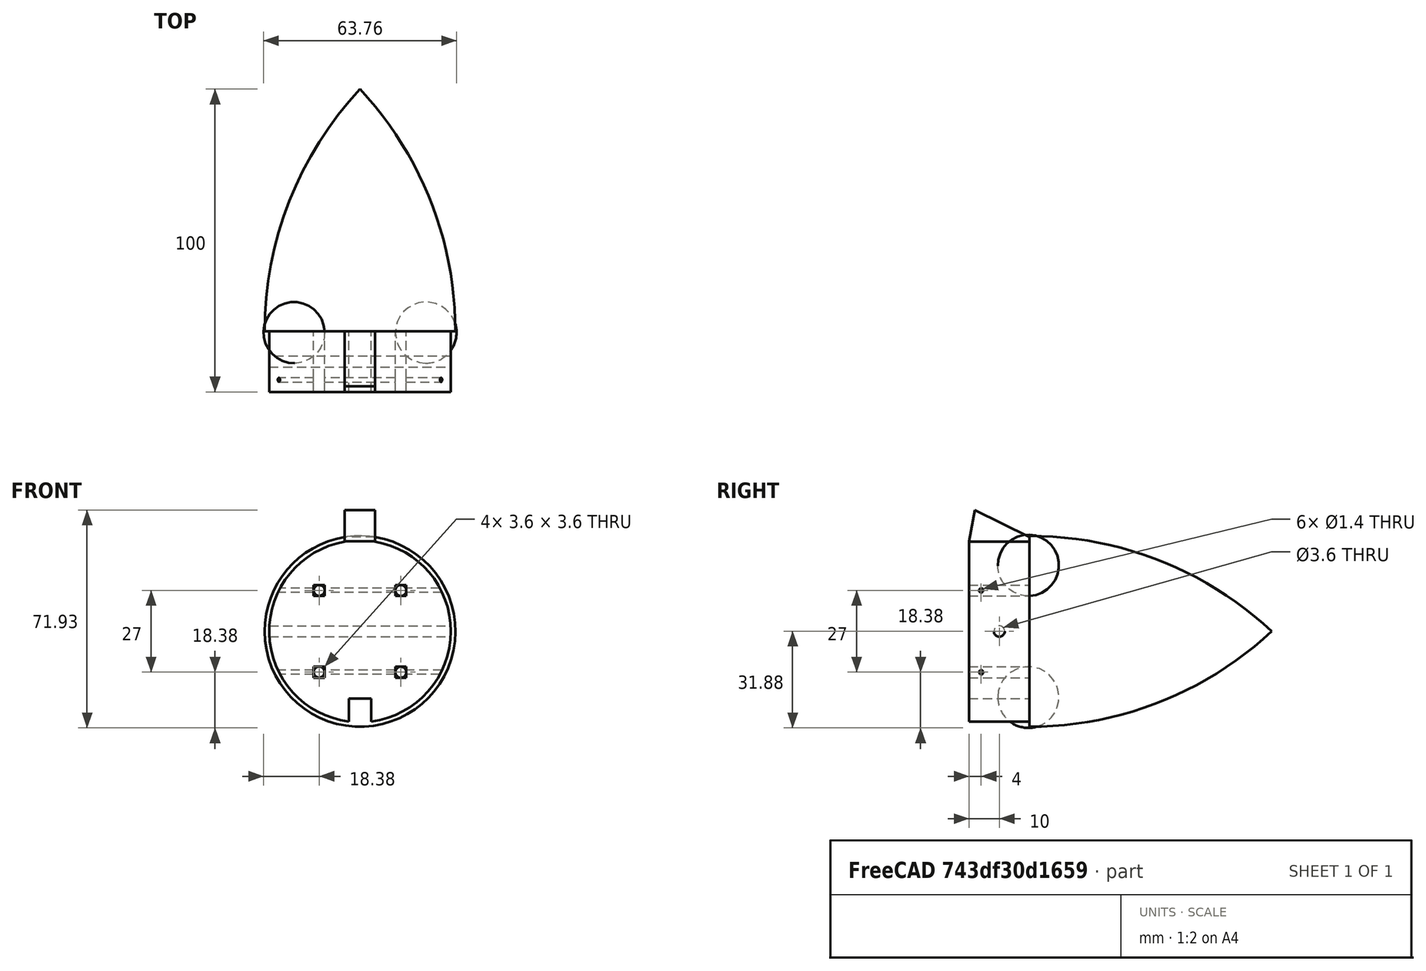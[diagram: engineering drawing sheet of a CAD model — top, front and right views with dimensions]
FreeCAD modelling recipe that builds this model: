
FCSTD DOCUMENT  (FreeCAD 1.0R38641 +468 (Git))
Label: ogive_cam-63
License: All rights reserved
LicenseURL: https://en.wikipedia.org/wiki/All_rights_reserved
objects: Sketcher::SketchObject×11, PartDesign::Pocket×7, PartDesign::Pad×2, PartDesign::Revolution×1, PartDesign::CoordinateSystem×1, PartDesign::Groove×1, PartDesign::PolarPattern×1, PartDesign::Body×1, Mesh::Feature×1
note: 59 computed .brp shape members not serialized (recipe doc carries the construction recipe); baked Part::Feature solids carry a one-line shape summary decoded from their .brp

FEATURE [Sketcher::SketchObject] Sketch
  ArcFitTolerance = 1e-06
  AttachmentSupport = -> [XY_Plane]
  FullyConstrained = false
  MakeInternals = false
  MapMode = 5
  sketch-geometry (4):
    g0: LineSegment StartX=0 StartY=0 StartZ=0 EndX=-31.5 EndY=0 EndZ=0
    g1: LineSegment StartX=-31.5 StartY=0 StartZ=0 EndX=-31.5 EndY=0.0739397 EndZ=0
    g2: ArcOfCircle CenterX=85.6496 CenterY=0.0739397 CenterZ=0 NormalX=0 NormalY=0 NormalZ=1 AngleXU=0 Radius=117.15 StartAngle=2.39075 EndAngle=3.14159
    g3: LineSegment StartX=2.132e-13 StartY=80 StartZ=0 EndX=0 EndY=0 EndZ=0
  constraints (10):
    c: Coincident(g-1,g0)
    c: PointOnObject(g0,g-1)
    c: Coincident(g0,g1)
    c: Vertical(g1)
    c: Tangent(g1,g2) = 1.5708
    c: PointOnObject(g2,g-2)
    c: Coincident(g2,g3)
    c: Coincident(g3,g0)
    c: DistanceY(g3,g3) = 80
    c: DistanceX(g0,g0) = 31.5
FEATURE [PartDesign::Revolution] Revolution
  Angle = 360
  Angle2 = 60
  Axis = (0,1,0)
  Base = (0,0,0)
  Profile = -> Sketch
  ReferenceAxis = -> Sketch [V_Axis]
  Refine = true
  Suppressed = false
  Type = 0
FEATURE [Sketcher::SketchObject] Sketch001
  ArcFitTolerance = 1e-06
  AttachmentSupport = -> [Revolution]
  FullyConstrained = true
  MakeInternals = false
  MapMode = 5
  Placement = pos=(0,0,0) rot=(1,0,0;1.5708rad)
  sketch-geometry (1):
    g0: Circle CenterX=0 CenterY=0 CenterZ=0 NormalX=0 NormalY=0 NormalZ=1 AngleXU=0 Radius=30
  constraints (2):
    c: Diameter(g0) = 60
    c: Coincident(g0,g-1)
FEATURE [PartDesign::Pad] Pad
  BaseFeature = -> Revolution
  Direction = (0,-1,2e-16)
  Length = 20
  Length2 = 10
  Profile = -> Sketch001
  ReferenceAxis = -> Sketch001 [N_Axis]
  Refine = true
  Suppressed = false
  Type = 0
FEATURE [Sketcher::SketchObject] Sketch002
  ArcFitTolerance = 1e-06
  AttachmentSupport = -> [Pad]
  FullyConstrained = false
  MakeInternals = false
  MapMode = 5
  Placement = pos=(0,-20,0) rot=(1,0,0;1.5708rad)
  sketch-geometry (4):
    g0: LineSegment StartX=-5.0789 StartY=29 StartZ=0 EndX=4.9211 EndY=29 EndZ=0
    g1: LineSegment StartX=4.9211 StartY=29 StartZ=0 EndX=4.9211 EndY=41 EndZ=0
    g2: LineSegment StartX=4.9211 StartY=41 StartZ=0 EndX=-5.0789 EndY=41 EndZ=0
    g3: LineSegment StartX=-5.0789 StartY=41 StartZ=0 EndX=-5.0789 EndY=29 EndZ=0
  constraints (11):
    c: Coincident(g0,g1)
    c: Coincident(g1,g2)
    c: Coincident(g2,g3)
    c: Coincident(g3,g0)
    c: Horizontal(g0)
    c: Horizontal(g2)
    c: Vertical(g1)
    c: Vertical(g3)
    c: Distance(g1,g3) = 10
    c: Distance(g0,g2) = 12
    c: DistanceY(g-1,g0) = 29
FEATURE [PartDesign::Pad] Pad001
  BaseFeature = -> Pad
  Direction = (0,-1,2e-16)
  Length = 20
  Length2 = 10
  Profile = -> Sketch002
  ReferenceAxis = -> Sketch002 [N_Axis]
  Refine = true
  Reversed = true
  Suppressed = false
  Type = 0
FEATURE [Sketcher::SketchObject] Sketch003
  ArcFitTolerance = 1e-06
  AttachmentSupport = -> [Pad001]
  ExternalGeometry = -> [Pad001]
  FullyConstrained = true
  MakeInternals = false
  MapMode = 5
  Placement = pos=(4.9211,0,0) rot=(0.57735,0.57735,0.57735;2.0944rad)
  sketch-geometry (3):
    g0: LineSegment StartX=-20 StartY=41 StartZ=0 EndX=7.1e-15 EndY=31.1132 EndZ=0
    g1: LineSegment StartX=7.1e-15 StartY=31.1132 StartZ=0 EndX=9.1e-15 EndY=41 EndZ=0
    g2: LineSegment StartX=9.1e-15 StartY=41 StartZ=0 EndX=-20 EndY=41 EndZ=0
  constraints (6):
    c: Coincident(g0,g1)
    c: Coincident(g1,g2)
    c: Coincident(g2,g0)
    c: Coincident(g0,g-3)
    c: Coincident(g1,g-4)
    c: Coincident(g0,g-4)
FEATURE [PartDesign::Pocket] Pocket
  BaseFeature = -> Pad001
  Direction = (-1,0,0)
  Length = 5
  Length2 = 5
  Profile = -> Sketch003
  ReferenceAxis = -> Sketch003 [N_Axis]
  Refine = true
  Suppressed = false
  Type = 1
FEATURE [Sketcher::SketchObject] Sketch004
  ArcFitTolerance = 1e-06
  AttachmentSupport = -> [Pocket]
  FullyConstrained = false
  MakeInternals = false
  MapMode = 5
  Placement = pos=(4.9211,0,0) rot=(0.57735,0.57735,0.57735;2.0944rad)
  sketch-geometry (3):
    g0: LineSegment StartX=-17.9945 StartY=40.5217 StartZ=0 EndX=-20.023 EndY=40.9971 EndZ=0
    g1: LineSegment StartX=-20.023 StartY=40.9971 StartZ=0 EndX=-20.023 EndY=29.5553 EndZ=0
    g2: LineSegment StartX=-20.023 StartY=29.5553 StartZ=0 EndX=-17.9945 EndY=40.5217 EndZ=0
  constraints (4):
    c: Coincident(g0,g1)
    c: Vertical(g1)
    c: Coincident(g1,g2)
    c: Coincident(g2,g0)
FEATURE [PartDesign::Pocket] Pocket001
  BaseFeature = -> Pocket
  Direction = (-1,0,0)
  Length = 5
  Length2 = 5
  Profile = -> Sketch004
  ReferenceAxis = -> Sketch004 [N_Axis]
  Refine = true
  Suppressed = false
  Type = 1
FEATURE [Sketcher::SketchObject] Sketch005
  ArcFitTolerance = 1e-06
  AttachmentSupport = -> [Pocket001]
  FullyConstrained = true
  MakeInternals = false
  MapMode = 5
  Placement = pos=(0,-20,5e-15) rot=(1,0,0;1.5708rad)
  sketch-geometry (4):
    g0: LineSegment StartX=-3.7 StartY=-22.2 StartZ=0 EndX=-3.7 EndY=-30.2 EndZ=0
    g1: LineSegment StartX=-3.7 StartY=-30.2 StartZ=0 EndX=3.7 EndY=-30.2 EndZ=0
    g2: LineSegment StartX=3.7 StartY=-30.2 StartZ=0 EndX=3.7 EndY=-22.2 EndZ=0
    g3: LineSegment StartX=3.7 StartY=-22.2 StartZ=0 EndX=-3.7 EndY=-22.2 EndZ=0
  constraints (12):
    c: Coincident(g0,g1)
    c: Coincident(g1,g2)
    c: Coincident(g2,g3)
    c: Coincident(g3,g0)
    c: Vertical(g0)
    c: Vertical(g2)
    c: Horizontal(g1)
    c: Horizontal(g3)
    c: Distance(g0,g2) = 7.4
    c: Distance(g1,g3) = 8
    c: DistanceX(g0,g-1) = 3.7
    c: DistanceY(g0,g-1) = 22.2
FEATURE [PartDesign::Pocket] Pocket002
  BaseFeature = -> Pocket001
  Direction = (0,1,-2e-16)
  Length = 20
  Length2 = 5
  Profile = -> Sketch005
  ReferenceAxis = -> Sketch005 [N_Axis]
  Refine = true
  Suppressed = false
  Type = 0
FEATURE [Sketcher::SketchObject] Sketch006
  ArcFitTolerance = 1e-06
  AttachmentSupport = -> [Pocket002]
  FullyConstrained = true
  MakeInternals = false
  MapMode = 5
  Placement = pos=(0,-20,5e-15) rot=(1,0,0;1.5708rad)
  sketch-geometry (16):
    g0: LineSegment StartX=-15.3 StartY=-11.7 StartZ=0 EndX=-15.3 EndY=-15.3 EndZ=0
    g1: LineSegment StartX=-15.3 StartY=-15.3 StartZ=0 EndX=-11.7 EndY=-15.3 EndZ=0
    g2: LineSegment StartX=-11.7 StartY=-15.3 StartZ=0 EndX=-11.7 EndY=-11.7 EndZ=0
    g3: LineSegment StartX=-11.7 StartY=-11.7 StartZ=0 EndX=-15.3 EndY=-11.7 EndZ=0
    g4: LineSegment StartX=11.7 StartY=-11.7 StartZ=0 EndX=11.7 EndY=-15.3 EndZ=0
    g5: LineSegment StartX=11.7 StartY=-15.3 StartZ=0 EndX=15.3 EndY=-15.3 EndZ=0
    g6: LineSegment StartX=15.3 StartY=-15.3 StartZ=0 EndX=15.3 EndY=-11.7 EndZ=0
    g7: LineSegment StartX=15.3 StartY=-11.7 StartZ=0 EndX=11.7 EndY=-11.7 EndZ=0
    g8: LineSegment StartX=-15.3 StartY=15.3 StartZ=0 EndX=-15.3 EndY=11.7 EndZ=0
    g9: LineSegment StartX=-15.3 StartY=11.7 StartZ=0 EndX=-11.7 EndY=11.7 EndZ=0
    g10: LineSegment StartX=-11.7 StartY=11.7 StartZ=0 EndX=-11.7 EndY=15.3 EndZ=0
    g11: LineSegment StartX=-11.7 StartY=15.3 StartZ=0 EndX=-15.3 EndY=15.3 EndZ=0
    g12: LineSegment StartX=11.7 StartY=15.3 StartZ=0 EndX=11.7 EndY=11.7 EndZ=0
    g13: LineSegment StartX=11.7 StartY=11.7 StartZ=0 EndX=15.3 EndY=11.7 EndZ=0
    g14: LineSegment StartX=15.3 StartY=11.7 StartZ=0 EndX=15.3 EndY=15.3 EndZ=0
    g15: LineSegment StartX=15.3 StartY=15.3 StartZ=0 EndX=11.7 EndY=15.3 EndZ=0
  constraints (48):
    c: Coincident(g0,g1)
    c: Coincident(g1,g2)
    c: Coincident(g2,g3)
    c: Coincident(g3,g0)
    c: Vertical(g0)
    c: Vertical(g2)
    c: Horizontal(g1)
    c: Horizontal(g3)
    c: Distance(g0,g2) = 3.6
    c: Distance(g1,g3) = 3.6
    c: Coincident(g4,g5)
    c: Coincident(g5,g6)
    c: Coincident(g6,g7)
    c: Coincident(g7,g4)
    c: Vertical(g4)
    c: Vertical(g6)
    c: Horizontal(g5)
    c: Horizontal(g7)
    c: Distance(g4,g6) = 3.6
    c: Distance(g5,g7) = 3.6
    c: DistanceY(g2,g-1) = 11.7
    c: DistanceY(g4,g-1) = 11.7
    c: DistanceX(g2,g-1) = 11.7
    c: DistanceX(g-1,g4) = 11.7
    c: Coincident(g8,g9)
    c: Coincident(g9,g10)
    c: Coincident(g10,g11)
    c: Coincident(g11,g8)
    c: Vertical(g8)
    c: Vertical(g10)
    c: Horizontal(g9)
    c: Horizontal(g11)
    c: Distance(g8,g10) = 3.6
    c: Distance(g9,g11) = 3.6
    c: Coincident(g12,g13)
    c: Coincident(g13,g14)
    c: Coincident(g14,g15)
    c: Coincident(g15,g12)
    c: Vertical(g12)
    c: Vertical(g14)
    c: Horizontal(g13)
    c: Horizontal(g15)
    c: Distance(g12,g14) = 3.6
    c: Distance(g13,g15) = 3.6
    c: DistanceY(g-1,g9) = 11.7
    c: DistanceY(g-1,g12) = 11.7
    c: DistanceX(g9,g-1) = 11.7
    c: DistanceX(g-1,g12) = 11.7
FEATURE [PartDesign::Pocket] Pocket003
  BaseFeature = -> Pocket002
  Direction = (0,1,-2e-16)
  Length = 20
  Length2 = 5
  Profile = -> Sketch006
  ReferenceAxis = -> Sketch006 [N_Axis]
  Refine = true
  Suppressed = false
  Type = 0
FEATURE [Sketcher::SketchObject] Sketch007
  ArcFitTolerance = 1e-06
  AttachmentSupport = -> [Pocket003]
  FullyConstrained = true
  MakeInternals = false
  MapMode = 5
  Placement = pos=(-11.7,0,0) rot=(0.57735,-0.57735,-0.57735;2.0944rad)
  sketch-geometry (1):
    g0: Circle CenterX=16 CenterY=-13.5 CenterZ=0 NormalX=0 NormalY=0 NormalZ=1 AngleXU=0 Radius=0.7
  constraints (3):
    c: Diameter(g0) = 1.4
    c: DistanceY(g0,g-1) = 13.5
    c: DistanceX(g-1,g0) = 16
FEATURE [PartDesign::Pocket] Pocket004
  BaseFeature = -> Pocket003
  Direction = (1,0,0)
  Length = 5
  Length2 = 5
  Midplane = true
  Profile = -> Sketch007
  ReferenceAxis = -> Sketch007 [N_Axis]
  Refine = true
  Suppressed = false
  Type = 1
FEATURE [Sketcher::SketchObject] Sketch008
  ArcFitTolerance = 1e-06
  AttachmentSupport = -> [Pocket004]
  FullyConstrained = true
  MakeInternals = false
  MapMode = 5
  Placement = pos=(-11.7,0,0) rot=(0.57735,-0.57735,-0.57735;2.0944rad)
  sketch-geometry (1):
    g0: Circle CenterX=16 CenterY=13.5 CenterZ=0 NormalX=0 NormalY=0 NormalZ=1 AngleXU=0 Radius=0.7
  constraints (3):
    c: Diameter(g0) = 1.4
    c: DistanceX(g-1,g0) = 16
    c: DistanceY(g-1,g0) = 13.5
FEATURE [PartDesign::Pocket] Pocket005
  BaseFeature = -> Pocket004
  Direction = (1,0,0)
  Length = 5
  Length2 = 5
  Midplane = true
  Profile = -> Sketch008
  ReferenceAxis = -> Sketch008 [N_Axis]
  Refine = true
  Suppressed = false
  Type = 1
FEATURE [PartDesign::CoordinateSystem] Local_CS
  AttacherType = Attacher::AttachEngine3D
  AttachmentSupport = -> [Pocket005]
  MapMode = 5
  Placement = pos=(0,-20,5e-15) rot=(1,0,0;1.5708rad)
FEATURE [Sketcher::SketchObject] Sketch009
  ArcFitTolerance = 1e-06
  FullyConstrained = true
  MakeInternals = false
  Placement = pos=(0,0,0) rot=(0.57735,0.57735,0.57735;2.0944rad)
  sketch-geometry (1):
    g0: Circle CenterX=-10 CenterY=0 CenterZ=0 NormalX=0 NormalY=0 NormalZ=1 AngleXU=0 Radius=1.8
  constraints (3):
    c: Diameter(g0) = 3.6
    c: PointOnObject(g0,g-1)
    c: DistanceX(g0,g-1) = 10
FEATURE [PartDesign::Pocket] Pocket006
  BaseFeature = -> Pocket005
  Direction = (-1,0,0)
  Length = 5
  Length2 = 5
  Midplane = true
  Profile = -> Sketch009
  ReferenceAxis = -> Sketch009 [N_Axis]
  Refine = true
  Suppressed = false
  Type = 1
FEATURE [Sketcher::SketchObject] Sketch010
  ArcFitTolerance = 1e-06
  AttachmentOffset = pos=(0,0,1.8) rot=(0,0,1;0rad)
  AttachmentSupport = -> [Pocket006]
  ExternalGeometry = -> [Sketch006]
  FullyConstrained = false
  MakeInternals = false
  MapMode = 5
  Placement = pos=(0,2.6e-15,13.5) rot=(0,0,1;0rad)
  sketch-geometry (4):
    g0: LineSegment StartX=-15.3 StartY=-1.11477 StartZ=0 EndX=-15.3 EndY=-0.404722 EndZ=0
    g1: ArcOfCircle CenterX=-5.20806 CenterY=-0.404722 CenterZ=0 NormalX=0 NormalY=0 NormalZ=1 AngleXU=0 Radius=10.0919 StartAngle=2.53508 EndAngle=3.14159
    g2: LineSegment StartX=-13.5 StartY=5.34775 StartZ=0 EndX=-13.5 EndY=-1.11477 EndZ=0
    g3: LineSegment StartX=-15.3 StartY=-1.11477 StartZ=0 EndX=-13.5 EndY=-1.11477 EndZ=0
  constraints (9):
    c: Vertical(g0)
    c: Tangent(g0,g1) = 1.5708
    c: Coincident(g2,g1)
    c: Vertical(g2)
    c: Coincident(g3,g0)
    c: Coincident(g3,g2)
    c: Horizontal(g3)
    c: DistanceX(g3,g3) = 1.8
    c: DistanceX(g0,g-3) = 0
FEATURE [PartDesign::Groove] Groove
  Angle = 360
  Angle2 = 60
  Axis = (0,-1,0)
  Base = (-13.5,5.34775,13.5)
  BaseFeature = -> Pocket006
  Profile = -> Sketch010
  ReferenceAxis = -> Sketch010 [Edge3]
  Reversed = true
  Suppressed = false
  Type = 0
FEATURE [PartDesign::PolarPattern] PolarPattern
  Angle = 360
  Axis = -> Y_Axis
  BaseFeature = -> Groove
  Mode = 0
  Occurrences = 4
  Offset = 120
  Originals = -> [Groove]
  Suppressed = false
  TransformMode = 0
FEATURE [PartDesign::Body] Body  label="Corps"
  AllowCompound = false
  Group = -> [Sketch,Revolution,Sketch001,Pad,Sketch002,Pad001,Sketch003,Pocket,Sketch004,Pocket001,Sketch005,Pocket002,Sketch006,Pocket003,Sketch007,Pocket004,Sketch008,Pocket005,Local_CS,Sketch009,Pocket006,Sketch010,Groove,PolarPattern]
  Origin = -> Origin
  Tip = -> PolarPattern
FEATURE [Mesh::Feature] Mesh  label="PolarPattern (Meshed)"
